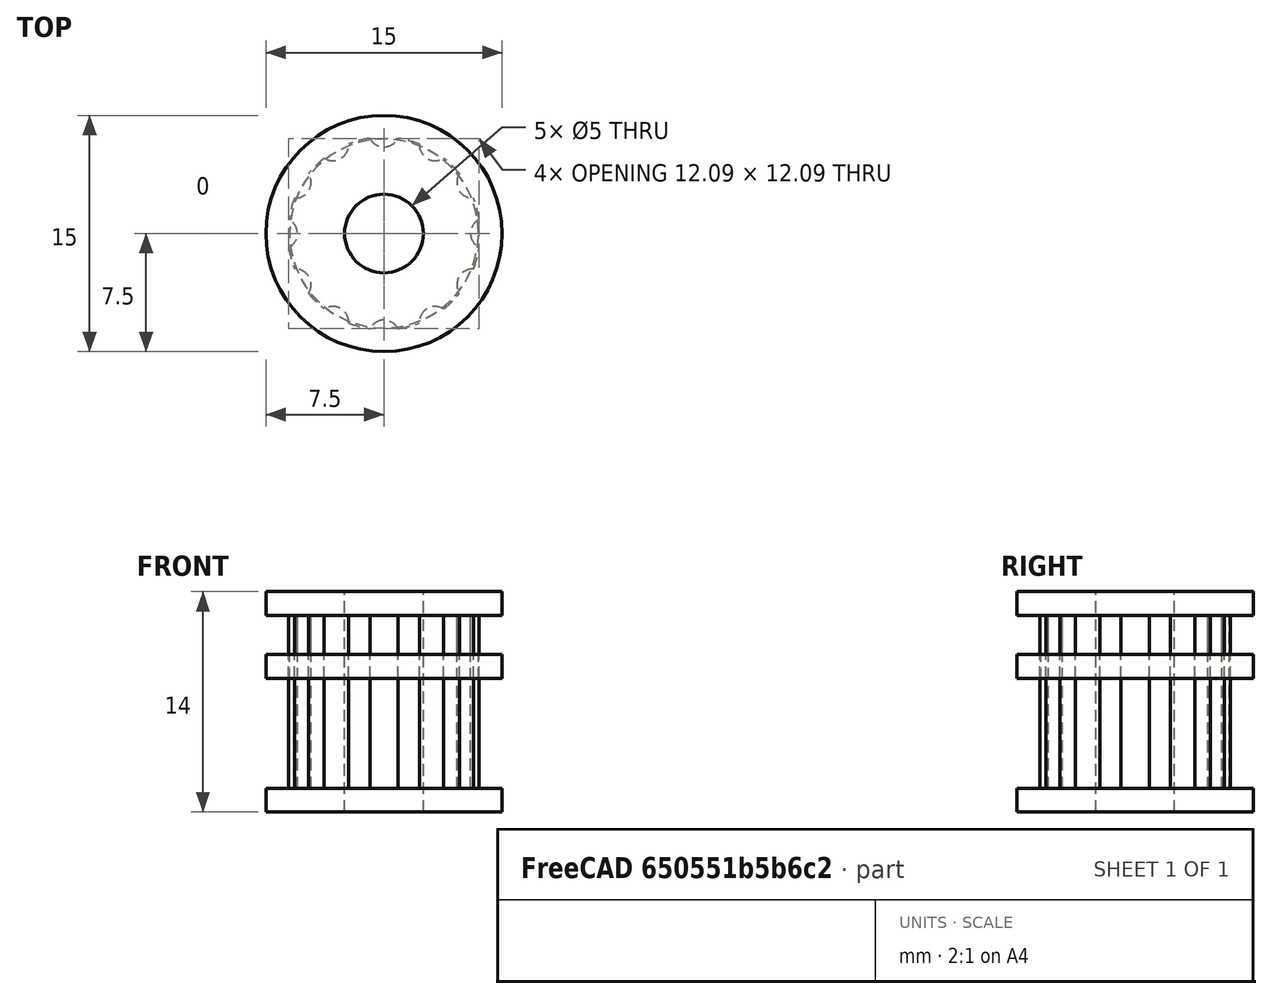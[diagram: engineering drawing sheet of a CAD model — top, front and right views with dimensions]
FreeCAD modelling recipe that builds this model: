
FCSTD DOCUMENT  (FreeCAD 0.18R16146 (Git))
Label: idler
License: Other
LicenseURL: GPL3
objects: Part::Feature×16, Part::Cylinder×5, Part::MultiFuse×3, Part::Cut×2
note: 26 computed .brp shape members not serialized (recipe doc carries the construction recipe); baked Part::Feature solids carry a one-line shape summary decoded from their .brp

FEATURE [Part::Cylinder] Cylinder
  Angle = 360
  AttacherType = Attacher::AttachEngine3D
  Height = 1.5
  Radius = 7.5
FEATURE [Part::Cylinder] Cylinder001
  Angle = 360
  AttacherType = Attacher::AttachEngine3D
  Height = 14
  Radius = 6.11
FEATURE [Part::Cylinder] Cylinder002
  Angle = 360
  AttacherType = Attacher::AttachEngine3D
  Height = 1.5
  Placement = pos=(0,0,12.5) rot=(0,0,1;0rad)
  Radius = 7.5
FEATURE [Part::Cylinder] Cylinder003
  Angle = 360
  AttacherType = Attacher::AttachEngine3D
  Height = 14
  Radius = 2.5
FEATURE [Part::Feature] Cut001  label="smooth-idler-6mm"
  shape: bbox 15 x 15 x 10 mm, 8 faces (baked)
FEATURE [Part::Cylinder] Cylinder004
  Angle = 360
  AttacherType = Attacher::AttachEngine3D
  Height = 10
  Placement = pos=(0,6.5,0) rot=(0,0,1;0rad)
  Radius = 1
FEATURE [Part::Feature] Cylinder004001  label="Cylinder005"
  Placement = pos=(0,0,0) rot=(0,0,-1;0.523599rad)
  shape: bbox 2 x 2 x 10 mm, 3 faces (baked)
FEATURE [Part::Feature] Cylinder004002  label="Cylinder006"
  Placement = pos=(0,0,0) rot=(0,0,-1;1.0472rad)
  shape: bbox 2 x 2 x 10 mm, 3 faces (baked)
FEATURE [Part::Feature] Cylinder004003  label="Cylinder007"
  Placement = pos=(0,0,0) rot=(0,0,1;0.523599rad)
  shape: bbox 2 x 2 x 10 mm, 3 faces (baked)
FEATURE [Part::Feature] Cylinder004004  label="Cylinder008"
  Placement = pos=(0,0,0) rot=(0,0,1;1.0472rad)
  shape: bbox 2 x 2 x 10 mm, 3 faces (baked)
FEATURE [Part::Feature] Cylinder004005  label="Cylinder009"
  Placement = pos=(0,0,0) rot=(0,0,1;1.5708rad)
  shape: bbox 2 x 2 x 10 mm, 3 faces (baked)
FEATURE [Part::Feature] Cylinder004006  label="Cylinder010"
  Placement = pos=(0,0,0) rot=(0,0,1;2.0944rad)
  shape: bbox 2 x 2 x 10 mm, 3 faces (baked)
FEATURE [Part::Feature] Cylinder004007  label="Cylinder011"
  Placement = pos=(0,0,0) rot=(0,0,-1;1.5708rad)
  shape: bbox 2 x 2 x 10 mm, 3 faces (baked)
FEATURE [Part::Feature] Cylinder004008  label="Cylinder012"
  Placement = pos=(0,0,0) rot=(0,0,-1;2.0944rad)
  shape: bbox 2 x 2 x 10 mm, 3 faces (baked)
FEATURE [Part::Feature] Cylinder004009  label="Cylinder013"
  Placement = pos=(0,0,0) rot=(0,0,1;3.66519rad)
  shape: bbox 2 x 2 x 10 mm, 3 faces (baked)
FEATURE [Part::Feature] Cylinder004010  label="Cylinder014"
  Placement = pos=(0,0,0) rot=(0,0,1;3.14159rad)
  shape: bbox 2 x 2 x 10 mm, 3 faces (baked)
FEATURE [Part::Feature] Cylinder004011  label="Cylinder015"
  Placement = pos=(0,0,0) rot=(0,0,1;2.61799rad)
  shape: bbox 2 x 2 x 10 mm, 3 faces (baked)
FEATURE [Part::Feature] Cut002001  label="tooth-idler-6mm"
  shape: bbox 15 x 15 x 10 mm, 31 faces (baked)
FEATURE [Part::MultiFuse] Fusion
  Shapes = -> [Cylinder004,Cylinder004001,Cylinder004002,Cylinder004003,Cylinder004004,Cylinder004005,Cylinder004006,Cylinder004007,Cylinder004008,Cylinder004009,Cylinder004010,Cylinder004011]
FEATURE [Part::Feature] Fusion001
  Placement = pos=(0,0,10) rot=(0,0,1;0rad)
  shape: bbox 15 x 15 x 10 mm, 36 faces, 12 solids (baked)
FEATURE [Part::MultiFuse] Fusion002  label="tooth-cut"
  Shapes = -> [Fusion001,Fusion]
FEATURE [Part::Feature] Cut002002  label="smooth-idler-9mm"
  shape: bbox 15 x 15 x 14 mm, 8 faces (baked)
FEATURE [Part::Cut] Cut
  Base = -> Cylinder001
  Tool = -> Fusion002
FEATURE [Part::MultiFuse] Fusion003
  Shapes = -> [Cylinder002,Cut,Cylinder]
FEATURE [Part::Cut] Cut002003
  Base = -> Fusion003
  Tool = -> Cylinder003
FEATURE [Part::Feature] Cut002003001  label="tooth-idler-9mm"
  shape: bbox 15 x 15 x 14 mm, 31 faces (baked)
